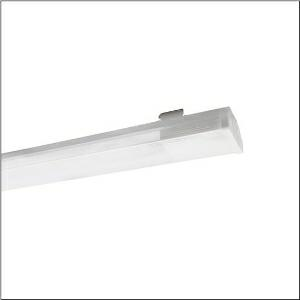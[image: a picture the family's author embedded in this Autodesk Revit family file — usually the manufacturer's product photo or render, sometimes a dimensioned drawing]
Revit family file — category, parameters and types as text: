
# Revit family: modario_r__31_gen_2_53bm812du4l3d2_13ed
name_source: partatom
category: Lighting Fixtures
units: mm (PartAtom-declared; Revit-internal decimal feet)

## family parameters
Cut with Voids When Loaded = No
Host = Face
Light Source = No
Part Type = Normal
Room Calculation Point = No
Round Connector Dimension = Use Diameter
Shared = No

## types (1)
- --- (1 x LED, 23600 lm, 128.4 W, 4000K)
    Apparent Load = 128 VA
    CIE Flux Codes = 47 80 95 93 100
    Color Rendering = 80
    Color Temperature = 4000K
    Default Elevation = 1800 mm
    Description = Modario® 31 Gen.2, luminaire insert, of sheet steel, coil coated, white, length: 2.392mm, width: 81mm, height: 82mm, 8x system unit, system units: 299mm, LED rated luminous flux: 23.600lm, light colour: 840, control gear: DALI 2, control gear: ECG DALI, with plug, 5-pole, with phase selection, mains connection: 220..240V, AC, 50/60Hz, rated input power: 128W, through-wiring accessed according to module size, primary optical cover: cover, of PMMA, light emission: direct distribution, primary light characteristic: symmetric, protection rating (complete): IP20, protection rating (LED compartment): IP50, insulation class (complete): insulation class I (protective earthing), certification: CE, ENEC, VDE, UKCA, impact resistance: IK03, permissible ambient temperature for indoor applications: -40..+35°C, corresponds to IFS (International Featured Standards) requirements for safety and quality in the food industry, reducing of maximum allowable ambient temperature of 5°C with ceiling mounting, packaging unit: 1 piece
    Height = 92 mm
    Lamp = 1 x LED
    Lamp Light Flux = 23600 lm
    Lamp Power = 128.4 W
    Lamp count = 1
    Length = 2392 mm
    Luminous efficacy = 184 lm/W
    Manufacturer = Siteco
    ModVariant = No
    Model = 53BM812DU4L3D2
    Mounting Place = Ceiling
    Mounting Type = Pendant
    Number of Poles = 1
    OnlyDefault = Yes
    Power Factor = 1
    Product Name = Modario® 31 Gen.2
    Product group = luminaire insert
    ProductGroupID = 902
    Protection Class = Protection class I
    Protection Degree = IP 20
    RLX_Detail_Level = 1
    RLX_Emergency_Light_Flux = 0 lm
    RLX_Emergency_Type = 0
    RLX_Emergency_Type_DB = No
    RlxData = <blob elided: 38285 chars, md5=0501cea3>
    Socket = socket
    Standby Power = 0 W
    System Light Flux = 23600 lm
    System Power = 128 W
    Type Comments = factory setting: luminous flux: 100 % | dim-lin: 254 | 594 mA
    Type Image = l_1341883.jpg
    URL = http://relux.com
    VarID = @adj_043466
    Voltage = 0 V
    Weight = 0.00 kg
    Width = 81 mm

## geometry (parser evidence)
native form markers: Blend x4, Sweep x13
no freeform markers — native parametric forms only
